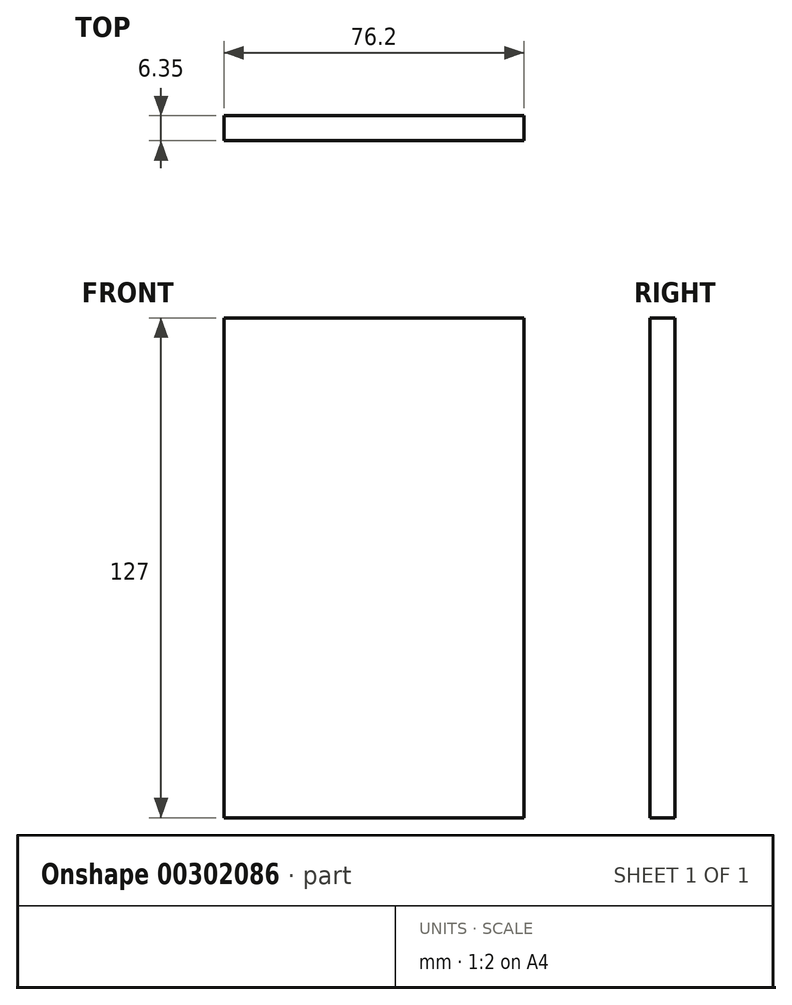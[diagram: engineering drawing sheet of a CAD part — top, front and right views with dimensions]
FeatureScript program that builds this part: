
annotation { "Feature Type Name" : "Feature", "Feature Type Description" : "" }
export const myFeature = defineFeature(function(context is Context, id is Id, definition is map)
    precondition{}
    {
        {
            var Q0;
            Q0=qCreatedBy(makeId("Front.planeOp"),FACE);
            var sketch = newSketch(context, id + "F0", { "sketchPlane" : qUnion([Q0])});
            skLineSegment(sketch, "E0.bottom", {"start": v(-31.62, 78.68) * mm, "end": v(44.58, 78.68) * mm});
            skLineSegment(sketch, "E0.top", {"start": v(-31.62, -48.32) * mm, "end": v(44.58, -48.32) * mm});
            skLineSegment(sketch, "E0.left", {"start": v(-31.62, 78.68) * mm, "end": v(-31.62, -48.32) * mm});
            skLineSegment(sketch, "E0.right", {"start": v(44.58, 78.68) * mm, "end": v(44.58, -48.32) * mm});
            skSolve(sketch);
        }
        {
            var Q0;
            Q0=makeQuery(id+"F0.imprint","IMPRINT",FACE,{"disambiguationData":[TD([[makeQuery(id+"F0.imprint","IMPRINT",EDGE,{"derivedFrom":sQuery(id+"F0.wireOp",EDGE,"E0.bottom")}),-1.0]])]});
            extrude(context, id + "F1", {"entities" : qUnion([Q0]), "depth" : 6.35 * mm});
        }
    });
